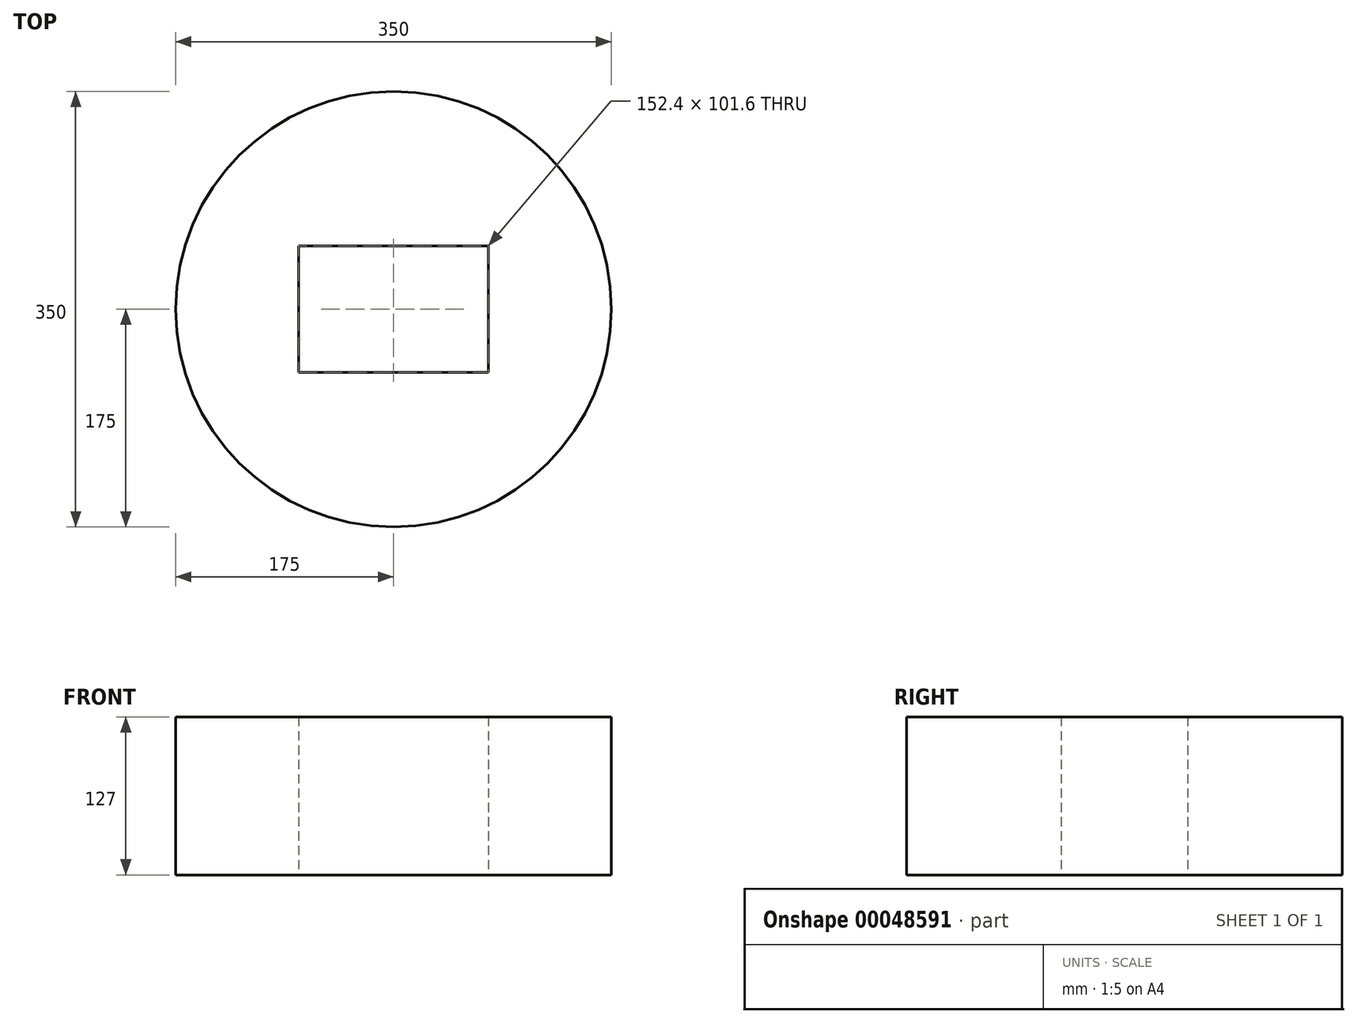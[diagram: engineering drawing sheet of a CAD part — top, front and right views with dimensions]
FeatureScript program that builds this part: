
annotation { "Feature Type Name" : "Feature", "Feature Type Description" : "" }
export const myFeature = defineFeature(function(context is Context, id is Id, definition is map)
    precondition{}
    {
        {
            var Q0;
            Q0=qCreatedBy(makeId("Top.planeOp"),FACE);
            var sketch = newSketch(context, id + "F0", { "sketchPlane" : qUnion([Q0])});
            skCircle(sketch, "E0", {"center": v(0, 0) * mm, "radius": 175 * mm});
            skLineSegment(sketch, "E1.rect.bottom", {"start": v(76.2, 50.8) * mm, "end": v(-76.2, 50.8) * mm});
            skLineSegment(sketch, "E1.rect.top", {"start": v(76.2, -50.8) * mm, "end": v(-76.2, -50.8) * mm});
            skLineSegment(sketch, "E1.rect.left", {"start": v(76.2, 50.8) * mm, "end": v(76.2, -50.8) * mm});
            skLineSegment(sketch, "E1.rect.right", {"start": v(-76.2, 50.8) * mm, "end": v(-76.2, -50.8) * mm});
            skSolve(sketch);
        }
        {
            var Q0;
            Q0=makeQuery(id+"F0.imprint","IMPRINT",FACE,{"disambiguationData":[TD([[makeQuery(id+"F0.imprint","IMPRINT",EDGE,{"derivedFrom":sQuery(id+"F0.wireOp",EDGE,"E0")}),1.0]])]});
            extrude(context, id + "F1", {"entities" : qUnion([Q0]), "depth" : 127 * mm});
        }
    });
